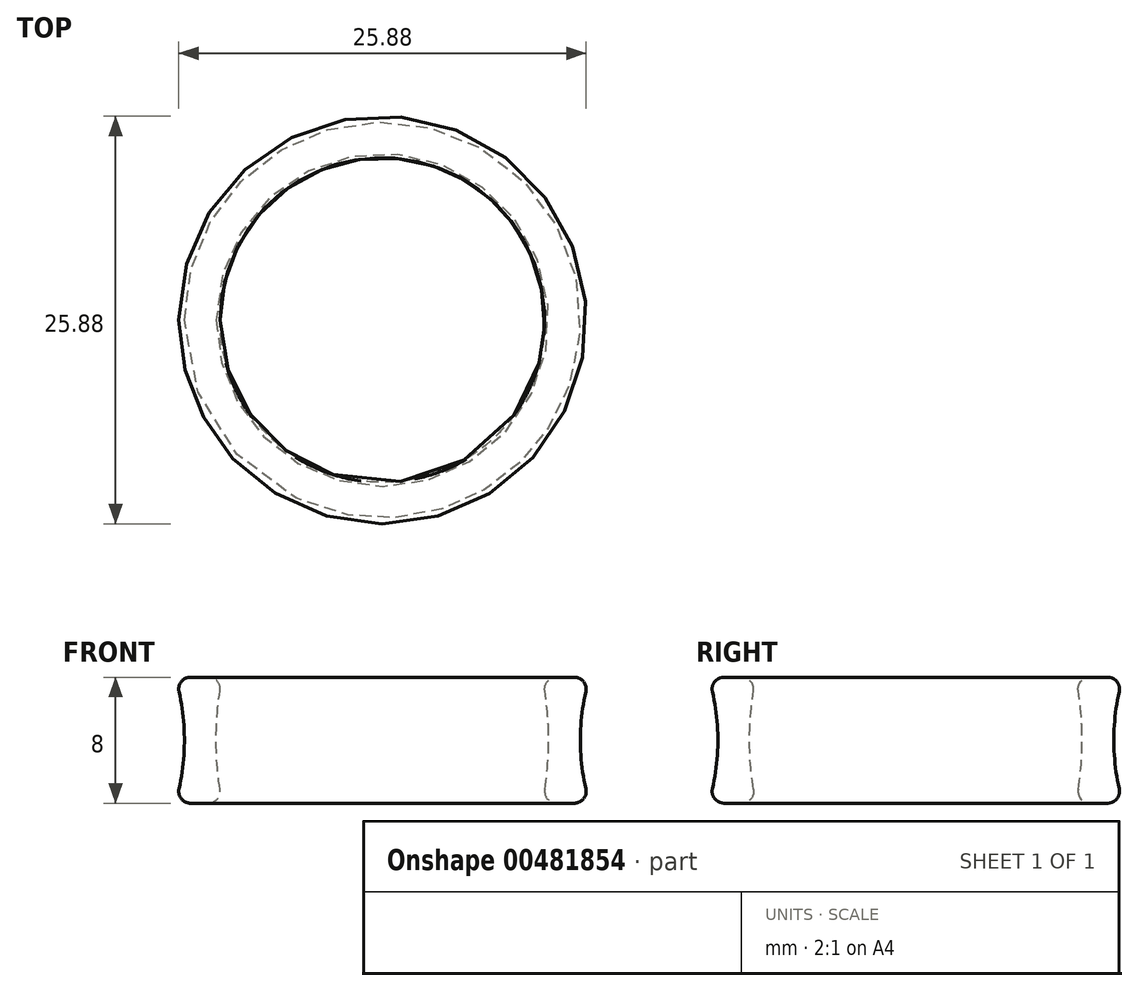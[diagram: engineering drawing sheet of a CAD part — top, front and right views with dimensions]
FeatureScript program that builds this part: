
annotation { "Feature Type Name" : "Feature", "Feature Type Description" : "" }
export const myFeature = defineFeature(function(context is Context, id is Id, definition is map)
    precondition{}
    {
        {
            var Q0;
            Q0=qCreatedBy(makeId("Front.planeOp"),FACE);
            var sketch = newSketch(context, id + "F0", { "sketchPlane" : qUnion([Q0])});
            skLineSegment(sketch, "E0", {"start": v(0, 0) * mm, "end": v(0, 7.56) * mm, "construction": true});
            skLineSegment(sketch, "E1", {"start": v(0, 0) * mm, "end": v(-35.38, 0) * mm, "construction": true});
            skLineSegment(sketch, "E2", {"start": v(-13.16, -4) * mm, "end": v(-13.16, 4) * mm, "construction": true});
            skLineSegment(sketch, "E3", {"start": v(-13.16, 4) * mm, "end": v(-10.16, 4) * mm, "construction": true});
            skLineSegment(sketch, "E4", {"start": v(-10.16, 4) * mm, "end": v(-10.16, 0) * mm, "construction": true});
            skLineSegment(sketch, "E5", {"start": v(-10.16, 0) * mm, "end": v(-10.16, -4) * mm, "construction": true});
            skLineSegment(sketch, "E6", {"start": v(-10.16, -4) * mm, "end": v(-13.16, -4) * mm, "construction": true});
            skArc(sketch, "E7", {"start": v(-10.31, 3.13) * mm, "mid": v(-10.56, 0) * mm, "end": v(-10.31, -3.13) * mm});
            skLineSegment(sketch, "E8", {"start": v(-11.06, 4) * mm, "end": v(-12.19, 4) * mm});
            skLineSegment(sketch, "E9", {"start": v(-12.19, -4) * mm, "end": v(-11.06, -4) * mm});
            skArc(sketch, "E10", {"start": v(-12.92, -3.08) * mm, "mid": v(-12.58, 0) * mm, "end": v(-12.92, 3.08) * mm});
            skPoint(sketch, "E11.visualSharp", {"position": v(-10.16, 4) * mm});
            skArc(sketch, "E11.filletArc", {"start": v(-10.31, 3.13) * mm, "mid": v(-10.49, 3.74) * mm, "end": v(-11.06, 4) * mm});
            skPoint(sketch, "E12.visualSharp", {"position": v(-10.16, -4) * mm});
            skArc(sketch, "E12.filletArc", {"start": v(-11.06, -4) * mm, "mid": v(-10.49, -3.74) * mm, "end": v(-10.31, -3.13) * mm});
            skPoint(sketch, "E13.visualSharp", {"position": v(-13.16, -4) * mm});
            skArc(sketch, "E13.filletArc", {"start": v(-12.92, -3.08) * mm, "mid": v(-12.77, -3.72) * mm, "end": v(-12.19, -4) * mm});
            skPoint(sketch, "E14.visualSharp", {"position": v(-13.16, 4) * mm});
            skArc(sketch, "E14.filletArc", {"start": v(-12.19, 4) * mm, "mid": v(-12.77, 3.72) * mm, "end": v(-12.92, 3.08) * mm});
            skSolve(sketch);
        }
        {
            var Q0;
            Q0 = qSketchRegion(id + "F0", true);
            var Q1;
            Q1=sQuery(id+"F0.wireOp",EDGE,"E0");
            revolve(context, id + "F1", {"entities" : qUnion([Q0]), "axis" : qUnion([Q1]), "revolveType" : RevolveType.FULL});
        }
    });
